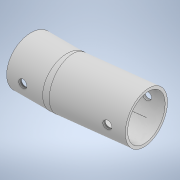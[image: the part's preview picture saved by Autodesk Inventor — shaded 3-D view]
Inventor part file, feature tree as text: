
AUTODESK INVENTOR PART (.ipt)
format: ipt  version: 2022 (Build 260153000, 153)  size: 242,688 bytes
history: native  units: mm
features: sketch x4, extrude x2, sweep x1
ambient origin geometry x8: Origin, YZ Plane, XZ Plane, XY Plane, X Axis, Y Axis, Z Axis, Center Point
bodies: Body1 (feature_tree)
feature tree (7):
  sweep  "Sweep1"
  extrude  "Extrusion8"  Depth=30.194196mm
  extrude  "Extrusion9"  Depth=10.0mm
  sketch  "Sketch5"  dims[d31=34.456mm d122=14.0mm]
  sketch  "Sketch6"  dims[d123=26.0mm d124=30.194196mm]
  sketch  "Sketch7"  dims[d125=10.0mm d126=16.0mm]
  sketch  "Sketch8"  dims[d127=18.0mm d128=0.0mm d129=0.0mm d130=6.0mm d131=3.0mm d132=25.0mm d133=0.0mm d134=6.0mm d135=3.0mm d136=25.0mm d137=0.0mm d138=0.01mm d139=0.01mm]
